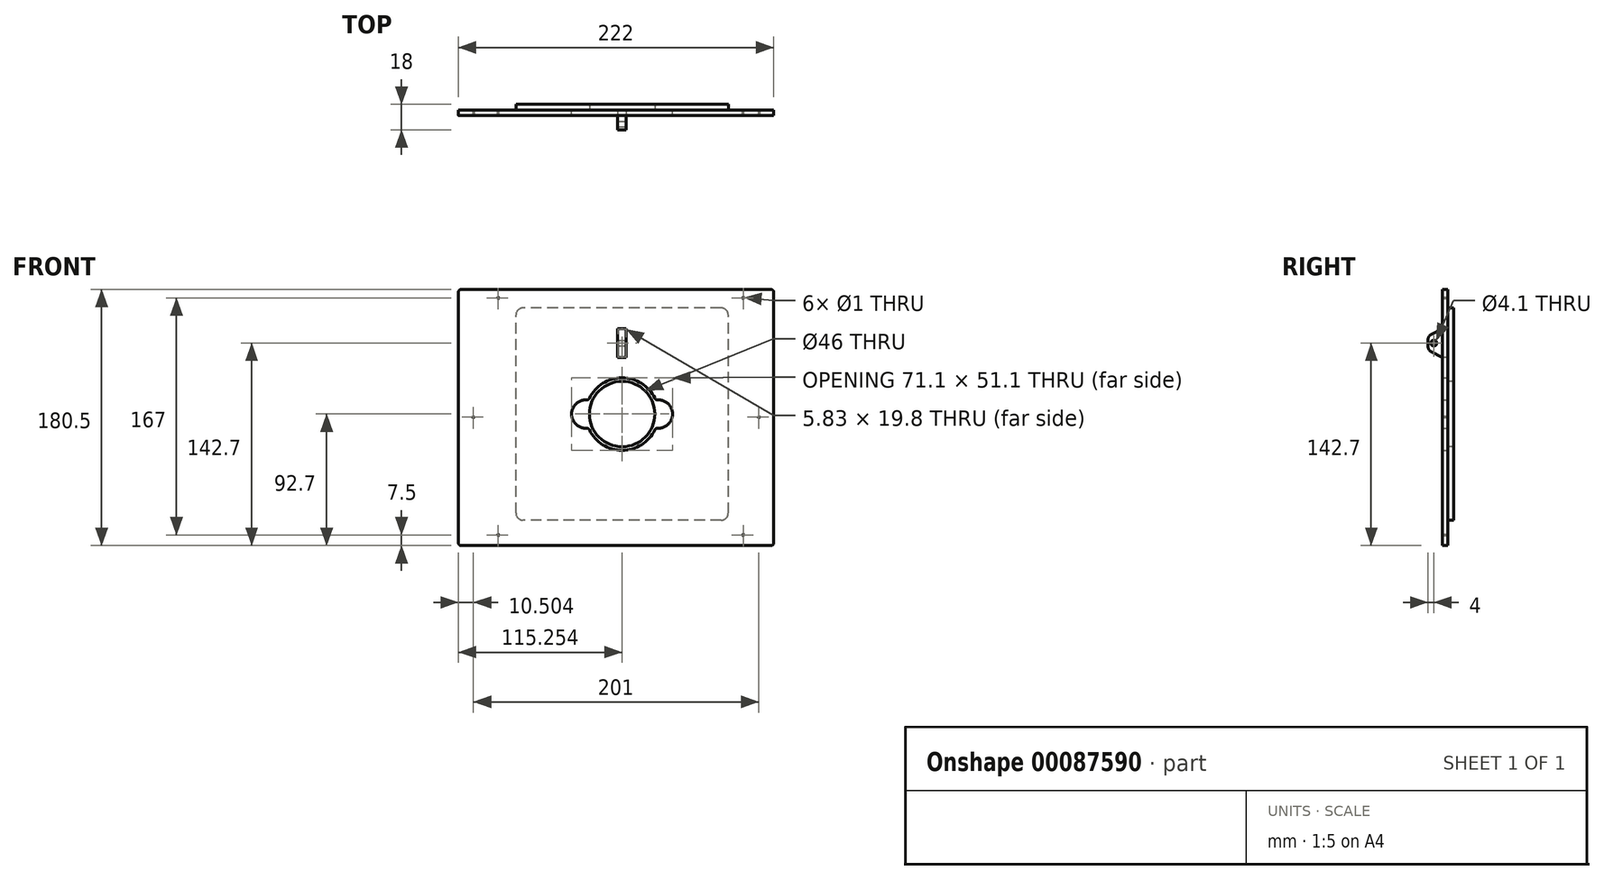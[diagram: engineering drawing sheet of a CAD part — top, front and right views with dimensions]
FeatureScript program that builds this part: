
annotation { "Feature Type Name" : "Feature", "Feature Type Description" : "" }
export const myFeature = defineFeature(function(context is Context, id is Id, definition is map)
    precondition{}
    {
        {
            var Q0;
            Q0=qCreatedBy(makeId("Front.planeOp"),FACE);
            var sketch = newSketch(context, id + "F0", { "sketchPlane" : qUnion([Q0])});
            skLineSegment(sketch, "E0.bottom", {"start": v(-37.98, 90.25) * mm, "end": v(-255.98, 90.25) * mm});
            skLineSegment(sketch, "E0.top", {"start": v(-37.98, -90.25) * mm, "end": v(-255.98, -90.25) * mm});
            skLineSegment(sketch, "E0.left", {"start": v(-35.98, 88.25) * mm, "end": v(-35.98, -88.25) * mm});
            skLineSegment(sketch, "E0.right", {"start": v(-257.98, 88.25) * mm, "end": v(-257.98, -88.25) * mm});
            skLineSegment(sketch, "E1.bottom", {"start": v(-57.48, 84.25) * mm, "end": v(-229.98, 84.25) * mm, "construction": true});
            skLineSegment(sketch, "E1.top", {"start": v(-57.48, -82.75) * mm, "end": v(-229.98, -82.75) * mm, "construction": true});
            skLineSegment(sketch, "E1.left", {"start": v(-57.48, 84.25) * mm, "end": v(-57.48, -82.75) * mm, "construction": true});
            skLineSegment(sketch, "E1.right", {"start": v(-229.98, 84.25) * mm, "end": v(-229.98, -82.75) * mm, "construction": true});
            skPoint(sketch, "E1.middle", {"position": v(-143.48, 0) * mm});
            skLineSegment(sketch, "E2", {"start": v(-257.98, 0) * mm, "end": v(-35.98, 0) * mm, "construction": true});
            skLineSegment(sketch, "E3.bottom", {"start": v(-67.73, 77.45) * mm, "end": v(-217.73, 77.45) * mm, "construction": true});
            skLineSegment(sketch, "E3.top", {"start": v(-67.73, -72.55) * mm, "end": v(-217.73, -72.55) * mm, "construction": true});
            skLineSegment(sketch, "E3.left", {"start": v(-67.73, 77.45) * mm, "end": v(-67.73, -72.55) * mm, "construction": true});
            skLineSegment(sketch, "E3.right", {"start": v(-217.73, 77.45) * mm, "end": v(-217.73, -72.55) * mm, "construction": true});
            skPoint(sketch, "E3.middle", {"position": v(-142.73, 2.45) * mm});
            skPoint(sketch, "E4.visualSharp", {"position": v(-257.98, 90.25) * mm});
            skArc(sketch, "E4.filletArc", {"start": v(-255.98, 90.25) * mm, "mid": v(-257.4, 89.66) * mm, "end": v(-257.98, 88.25) * mm});
            skPoint(sketch, "E5.visualSharp", {"position": v(-257.98, -90.25) * mm});
            skArc(sketch, "E5.filletArc", {"start": v(-257.98, -88.25) * mm, "mid": v(-257.4, -89.66) * mm, "end": v(-255.98, -90.25) * mm});
            skPoint(sketch, "E6.visualSharp", {"position": v(-35.98, 90.25) * mm});
            skArc(sketch, "E6.filletArc", {"start": v(-35.98, 88.25) * mm, "mid": v(-36.56, 89.66) * mm, "end": v(-37.98, 90.25) * mm});
            skPoint(sketch, "E7.visualSharp", {"position": v(-35.98, -90.25) * mm});
            skArc(sketch, "E7.filletArc", {"start": v(-37.98, -90.25) * mm, "mid": v(-36.56, -89.66) * mm, "end": v(-35.98, -88.25) * mm});
            skCircle(sketch, "E8", {"center": v(-229.98, 84.25) * mm, "radius": 0.5 * mm});
            skCircle(sketch, "E9", {"center": v(-229.98, -82.75) * mm, "radius": 0.5 * mm});
            skCircle(sketch, "E10", {"center": v(-57.48, 84.25) * mm, "radius": 0.5 * mm});
            skCircle(sketch, "E11", {"center": v(-57.48, -82.75) * mm, "radius": 0.5 * mm});
            skLineSegment(sketch, "E12", {"start": v(-168.28, 2.45) * mm, "end": v(-117.18, 2.45) * mm, "construction": true});
            skArc(sketch, "E13", {"start": v(-167.66, 12.43) * mm, "mid": v(-178.28, 2.45) * mm, "end": v(-167.66, -7.53) * mm});
            skArc(sketch, "E14", {"start": v(-117.8, -7.53) * mm, "mid": v(-107.18, 2.45) * mm, "end": v(-117.8, 12.43) * mm});
            skArc(sketch, "E15.trimOffspring", {"start": v(-165.74, -8.66) * mm, "mid": v(-142.73, -23.1) * mm, "end": v(-119.72, -8.66) * mm});
            skArc(sketch, "E16.trimOffspring", {"start": v(-119.72, 13.56) * mm, "mid": v(-142.73, 28) * mm, "end": v(-165.74, 13.56) * mm});
            skPoint(sketch, "E17.visualSharp", {"position": v(-166.32, 12.26) * mm});
            skArc(sketch, "E17.filletArc", {"start": v(-167.66, 12.43) * mm, "mid": v(-166.53, 12.7) * mm, "end": v(-165.74, 13.56) * mm});
            skPoint(sketch, "E18.visualSharp", {"position": v(-166.32, -7.36) * mm});
            skArc(sketch, "E18.filletArc", {"start": v(-165.74, -8.66) * mm, "mid": v(-166.53, -7.8) * mm, "end": v(-167.66, -7.53) * mm});
            skPoint(sketch, "E19.visualSharp", {"position": v(-119.13, -7.36) * mm});
            skArc(sketch, "E19.filletArc", {"start": v(-117.8, -7.53) * mm, "mid": v(-118.93, -7.8) * mm, "end": v(-119.72, -8.66) * mm});
            skPoint(sketch, "E20.visualSharp", {"position": v(-119.13, 12.26) * mm});
            skArc(sketch, "E20.filletArc", {"start": v(-119.72, 13.56) * mm, "mid": v(-118.93, 12.7) * mm, "end": v(-117.8, 12.43) * mm});
            skLineSegment(sketch, "E21.bottom", {"start": v(-139.81, 42.55) * mm, "end": v(-145.64, 42.55) * mm});
            skLineSegment(sketch, "E21.top", {"start": v(-139.81, 62.35) * mm, "end": v(-145.64, 62.35) * mm});
            skLineSegment(sketch, "E21.left", {"start": v(-139.81, 42.55) * mm, "end": v(-139.81, 62.35) * mm});
            skLineSegment(sketch, "E21.right", {"start": v(-145.64, 42.55) * mm, "end": v(-145.64, 62.35) * mm});
            skPoint(sketch, "E21.middle", {"position": v(-142.73, 52.45) * mm});
            skSolve(sketch);
        }
        {
            var Q0;
            Q0 = qSketchRegion(id + "F0", true);
            extrude(context, id + "F1", {"entities" : qUnion([Q0]), "depth" : 4 * mm});
        }
        {
            var Q0;
            Q0=makeQuery(id+"F1.opExtrude","CAP_FACE",FACE,{"disambiguationData":[OSD([sQuery(id+"F0.wireOp",EDGE,"E0.bottom"),sQuery(id+"F0.wireOp",EDGE,"E0.top"),sQuery(id+"F0.wireOp",EDGE,"E0.left"),sQuery(id+"F0.wireOp",EDGE,"E0.right"),sQuery(id+"F0.wireOp",EDGE,"E4.filletArc"),sQuery(id+"F0.wireOp",EDGE,"E5.filletArc"),sQuery(id+"F0.wireOp",EDGE,"E6.filletArc"),sQuery(id+"F0.wireOp",EDGE,"E7.filletArc"),sQuery(id+"F0.wireOp",EDGE,"E8"),sQuery(id+"F0.wireOp",EDGE,"E9"),sQuery(id+"F0.wireOp",EDGE,"E10"),sQuery(id+"F0.wireOp",EDGE,"E11"),sQuery(id+"F0.wireOp",EDGE,"E13"),sQuery(id+"F0.wireOp",EDGE,"E14"),sQuery(id+"F0.wireOp",EDGE,"E15.trimOffspring"),sQuery(id+"F0.wireOp",EDGE,"E16.trimOffspring"),sQuery(id+"F0.wireOp",EDGE,"E17.filletArc"),sQuery(id+"F0.wireOp",EDGE,"E18.filletArc"),sQuery(id+"F0.wireOp",EDGE,"E19.filletArc"),sQuery(id+"F0.wireOp",EDGE,"E20.filletArc"),sQuery(id+"F0.wireOp",EDGE,"E21.bottom"),sQuery(id+"F0.wireOp",EDGE,"E21.top"),sQuery(id+"F0.wireOp",EDGE,"E21.left"),sQuery(id+"F0.wireOp",EDGE,"E21.right")])],"isStart":true});
            var sketch = newSketch(context, id + "F2", { "sketchPlane" : qUnion([Q0])});
            skArc(sketch, "E22.0", {"start": v(165.74, -8.66) * mm, "mid": v(142.73, -23.1) * mm, "end": v(119.72, -8.66) * mm, "construction": true});
            skCircle(sketch, "E23", {"center": v(142.73, 2.45) * mm, "radius": 23 * mm});
            skLineSegment(sketch, "E24.bottom", {"start": v(72.98, -72.3) * mm, "end": v(212.48, -72.3) * mm});
            skLineSegment(sketch, "E24.top", {"start": v(72.98, 77.2) * mm, "end": v(212.48, 77.2) * mm});
            skLineSegment(sketch, "E24.left", {"start": v(67.98, -67.3) * mm, "end": v(67.98, 72.2) * mm});
            skLineSegment(sketch, "E24.right", {"start": v(217.48, -67.3) * mm, "end": v(217.48, 72.2) * mm});
            skPoint(sketch, "E25.visualSharp", {"position": v(217.48, -72.3) * mm});
            skArc(sketch, "E25.filletArc", {"start": v(212.48, -72.3) * mm, "mid": v(216.01, -70.84) * mm, "end": v(217.48, -67.3) * mm});
            skPoint(sketch, "E26.visualSharp", {"position": v(217.48, 77.2) * mm});
            skArc(sketch, "E26.filletArc", {"start": v(217.48, 72.2) * mm, "mid": v(216.01, 75.74) * mm, "end": v(212.48, 77.2) * mm});
            skPoint(sketch, "E27.visualSharp", {"position": v(67.98, 77.2) * mm});
            skArc(sketch, "E27.filletArc", {"start": v(72.98, 77.2) * mm, "mid": v(69.44, 75.74) * mm, "end": v(67.98, 72.2) * mm});
            skPoint(sketch, "E28.visualSharp", {"position": v(67.98, -72.3) * mm});
            skArc(sketch, "E28.filletArc", {"start": v(67.98, -67.3) * mm, "mid": v(69.44, -70.84) * mm, "end": v(72.98, -72.3) * mm});
            skSolve(sketch);
        }
        {
            var Q0;
            Q0 = qSketchRegion(id + "F2", true);
            extrude(context, id + "F3", {"entities" : qUnion([Q0]), "depth" : 4 * mm});
        }
        {
            var Q0;
            Q0=makeQuery(id+"F1.opExtrude","SWEPT_FACE",FACE,{"disambiguationData":[OSD([sQuery(id+"F0.wireOp",EDGE,"E21.left")])]});
            var sketch = newSketch(context, id + "F4", { "sketchPlane" : qUnion([Q0])});
            skLineSegment(sketch, "E29.0", {"start": v(0, 42.55) * mm, "end": v(0, 62.35) * mm});
            skLineSegment(sketch, "E30", {"start": v(0, 62.35) * mm, "end": v(0, 62.55) * mm});
            skLineSegment(sketch, "E31", {"start": v(0, 42.55) * mm, "end": v(0, 42.35) * mm});
            skPoint(sketch, "E32.endSnap0", {"position": v(0, 52.45) * mm});
            skLineSegment(sketch, "E33", {"start": v(0, 62.55) * mm, "end": v(4, 62.55) * mm});
            skLineSegment(sketch, "E34", {"start": v(4, 62.55) * mm, "end": v(11.82, 58.56) * mm});
            skLineSegment(sketch, "E35", {"start": v(0, 42.35) * mm, "end": v(4, 42.35) * mm});
            skLineSegment(sketch, "E36", {"start": v(4, 42.35) * mm, "end": v(11.82, 46.34) * mm});
            skLineSegment(sketch, "E37", {"start": v(14, 52.45) * mm, "end": v(0, 52.45) * mm, "construction": true});
            skLineSegment(sketch, "E38", {"start": v(14, 55) * mm, "end": v(14, 49.9) * mm});
            skCircle(sketch, "E39", {"center": v(10, 52.45) * mm, "radius": 2.05 * mm});
            skPoint(sketch, "E40.visualSharp", {"position": v(14, 57.45) * mm});
            skArc(sketch, "E40.filletArc", {"start": v(14, 55) * mm, "mid": v(13.41, 57.09) * mm, "end": v(11.82, 58.56) * mm});
            skPoint(sketch, "E41.visualSharp", {"position": v(14, 47.45) * mm});
            skArc(sketch, "E41.filletArc", {"start": v(11.82, 46.34) * mm, "mid": v(13.41, 47.81) * mm, "end": v(14, 49.9) * mm});
            skSolve(sketch);
        }
        {
            var Q0;
            Q0=makeQuery(id+"F4.imprint","IMPRINT",FACE,{"disambiguationData":[TD([[makeQuery(id+"F4.imprint","IMPRINT",EDGE,{"derivedFrom":sQuery(id+"F4.wireOp",EDGE,"E30")}),-1.0]])]});
            var Q1;
            Q1=makeQuery(id+"F4.imprint","IMPRINT",FACE,{"disambiguationData":[TD([[makeQuery(id+"F4.imprint","IMPRINT",EDGE,{"derivedFrom":sQuery(id+"F4.wireOp",EDGE,"E29.0")}),-1.0]])]});
            extrude(context, id + "F5", {"entities" : qUnion([Q0, Q1]), "depth" : 6 * mm});
        }
        {
            var Q0;
            Q0=makeQuery(id+"F1.opExtrude","CAP_FACE",FACE,{"disambiguationData":[OSD([sQuery(id+"F0.wireOp",EDGE,"E0.bottom"),sQuery(id+"F0.wireOp",EDGE,"E0.top"),sQuery(id+"F0.wireOp",EDGE,"E0.left"),sQuery(id+"F0.wireOp",EDGE,"E0.right"),sQuery(id+"F0.wireOp",EDGE,"E4.filletArc"),sQuery(id+"F0.wireOp",EDGE,"E5.filletArc"),sQuery(id+"F0.wireOp",EDGE,"E6.filletArc"),sQuery(id+"F0.wireOp",EDGE,"E7.filletArc"),sQuery(id+"F0.wireOp",EDGE,"E8"),sQuery(id+"F0.wireOp",EDGE,"E9"),sQuery(id+"F0.wireOp",EDGE,"E10"),sQuery(id+"F0.wireOp",EDGE,"E11"),sQuery(id+"F0.wireOp",EDGE,"E13"),sQuery(id+"F0.wireOp",EDGE,"E14"),sQuery(id+"F0.wireOp",EDGE,"E15.trimOffspring"),sQuery(id+"F0.wireOp",EDGE,"E16.trimOffspring"),sQuery(id+"F0.wireOp",EDGE,"E17.filletArc"),sQuery(id+"F0.wireOp",EDGE,"E18.filletArc"),sQuery(id+"F0.wireOp",EDGE,"E19.filletArc"),sQuery(id+"F0.wireOp",EDGE,"E20.filletArc"),sQuery(id+"F0.wireOp",EDGE,"E21.bottom"),sQuery(id+"F0.wireOp",EDGE,"E21.top"),sQuery(id+"F0.wireOp",EDGE,"E21.left"),sQuery(id+"F0.wireOp",EDGE,"E21.right")])],"isStart":false});
            var sketch = newSketch(context, id + "F6", { "sketchPlane" : qUnion([Q0])});
            skLineSegment(sketch, "E42.0", {"start": v(-37.98, 90.25) * mm, "end": v(-255.98, 90.25) * mm, "construction": true});
            skLineSegment(sketch, "E42.1", {"start": v(-35.98, 88.25) * mm, "end": v(-35.98, -88.25) * mm, "construction": true});
            skCircle(sketch, "E43", {"center": v(-247.48, 0.25) * mm, "radius": 0.5 * mm});
            skCircle(sketch, "E44", {"center": v(-46.48, 0.25) * mm, "radius": 0.5 * mm});
            skLineSegment(sketch, "E45", {"start": v(-247.48, 0.25) * mm, "end": v(-46.48, 0.25) * mm, "construction": true});
            skLineSegment(sketch, "E46", {"start": v(-146.98, 90.25) * mm, "end": v(-146.98, 0.25) * mm, "construction": true});
            skSolve(sketch);
        }
        {
            var Q0;
            Q0 = qSketchRegion(id + "F6", true);
            extrude(context, id + "F7", {"entities" : qUnion([Q0]), "operationType" : NewBodyOperationType.REMOVE, "oppositeDirection" : true, "depth" : 25 * mm});
        }
    });
